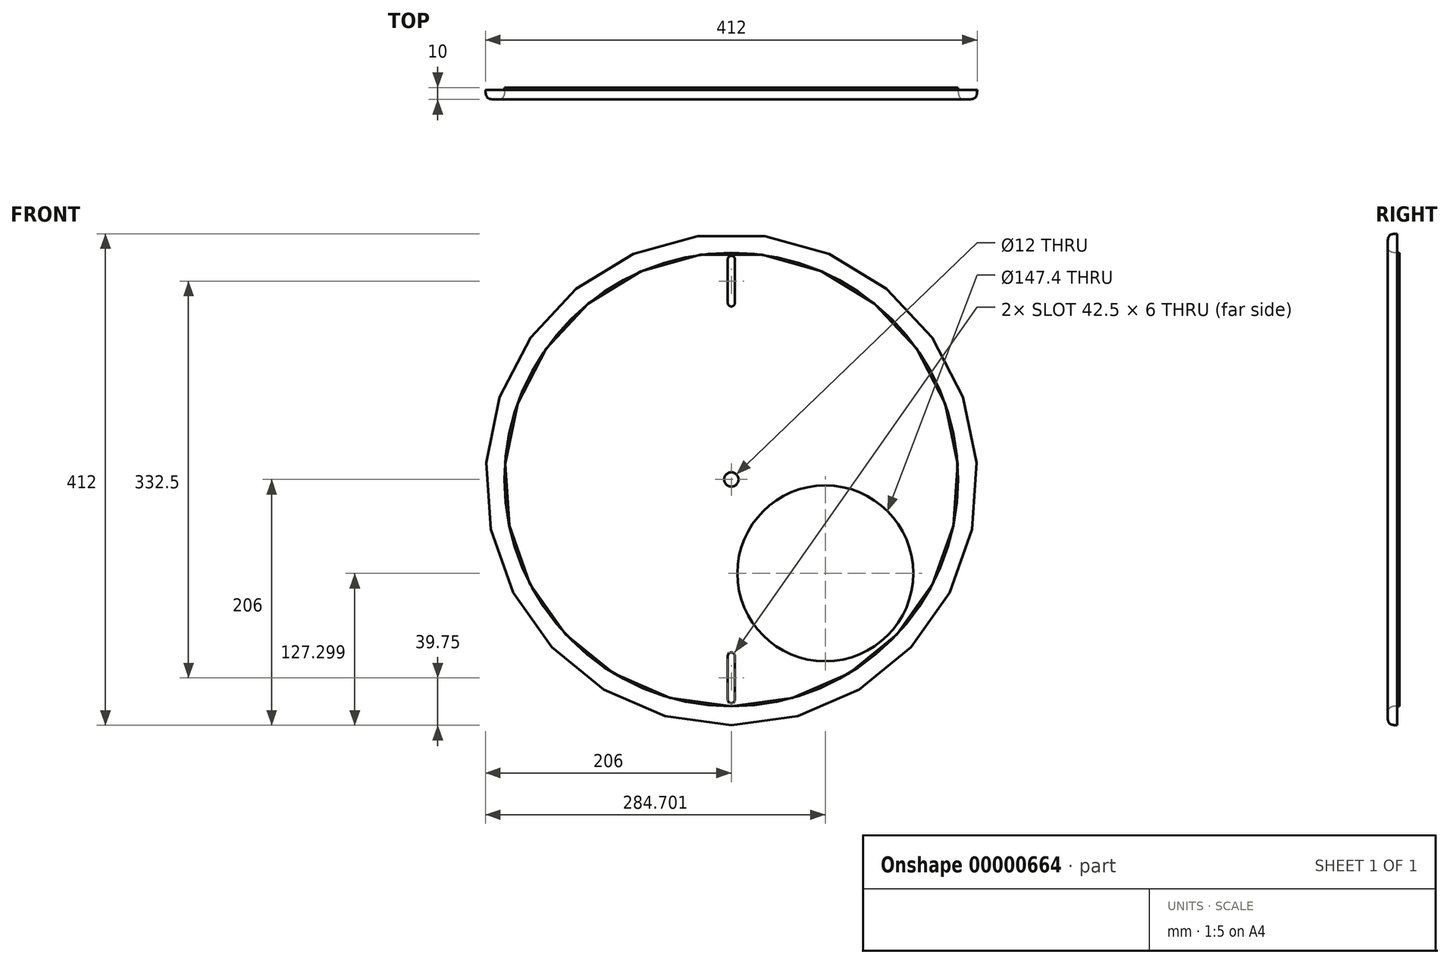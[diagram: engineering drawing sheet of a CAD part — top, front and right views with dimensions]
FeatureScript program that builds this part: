
annotation { "Feature Type Name" : "Feature", "Feature Type Description" : "" }
export const myFeature = defineFeature(function(context is Context, id is Id, definition is map)
    precondition{}
    {
        {
            var Q0;
            Q0=qCreatedBy(makeId("Front.planeOp"),FACE);
            var sketch = newSketch(context, id + "F0", { "sketchPlane" : qUnion([Q0])});
            skCircle(sketch, "E0", {"center": v(0, 0) * mm, "radius": 190 * mm});
            skCircle(sketch, "E1", {"center": v(0, 0) * mm, "radius": 6 * mm});
            skLineSegment(sketch, "E2", {"start": v(0, 190) * mm, "end": v(0, -190) * mm, "construction": true});
            skLineSegment(sketch, "E3", {"start": v(-190, 0) * mm, "end": v(190, 0) * mm, "construction": true});
            skCircle(sketch, "E4", {"center": v(78.7, -78.7) * mm, "radius": 78.7 * mm, "construction": true});
            skCircle(sketch, "E5", {"center": v(0, 0) * mm, "radius": 142.5 * mm, "construction": true});
            skCircle(sketch, "E6", {"center": v(0, 0) * mm, "radius": 145 * mm, "construction": true});
            skCircle(sketch, "E7", {"center": v(0, 0) * mm, "radius": 187.5 * mm, "construction": true});
            skLineSegment(sketch, "E8", {"start": v(0, 187.5) * mm, "end": v(0, 145) * mm, "construction": true});
            skLineSegment(sketch, "E9.rect.left", {"start": v(3, 184.5) * mm, "end": v(3, 148) * mm});
            skLineSegment(sketch, "E9.rect.right", {"start": v(-3, 184.5) * mm, "end": v(-3, 148) * mm});
            skPoint(sketch, "E9.rect.middle", {"position": v(0, 166.25) * mm});
            skArc(sketch, "E10", {"start": v(-3, 148) * mm, "mid": v(0, 145) * mm, "end": v(3, 148) * mm});
            skArc(sketch, "E11", {"start": v(3, 184.5) * mm, "mid": v(0, 187.5) * mm, "end": v(-3, 184.5) * mm});
            skPoint(sketch, "E12.orphan", {"position": v(3, 145.02) * mm});
            skPoint(sketch, "E13.orphan", {"position": v(-3, 145.02) * mm});
            skPoint(sketch, "E14.orphan", {"position": v(-3, 187.48) * mm});
            skPoint(sketch, "E15.orphan", {"position": v(3, 187.48) * mm});
            skArc(sketch, "E16.0.MirrorCS", {"start": v(-3, -148) * mm, "mid": v(0, -145) * mm, "end": v(3, -148) * mm});
            skArc(sketch, "E16.1.MirrorCS", {"start": v(3, -184.5) * mm, "mid": v(0, -187.5) * mm, "end": v(-3, -184.5) * mm});
            skLineSegment(sketch, "E16.2.MirrorCS", {"start": v(-3, -184.5) * mm, "end": v(-3, -148) * mm});
            skLineSegment(sketch, "E16.3.MirrorCS", {"start": v(3, -184.5) * mm, "end": v(3, -148) * mm});
            skCircle(sketch, "E17.0", {"center": v(78.7, -78.7) * mm, "radius": 73.7 * mm});
            skSolve(sketch);
        }
        {
            var Q0;
            Q0=makeQuery(id+"F0.imprint","IMPRINT",FACE,{"disambiguationData":[TD([[makeQuery(id+"F0.imprint","IMPRINT",EDGE,{"derivedFrom":sQuery(id+"F0.wireOp",EDGE,"E0")}),1.0]])]});
            extrude(context, id + "F1", {"entities" : qUnion([Q0]), "depth" : 2 * mm});
        }
        {
            var Q0;
            Q0=makeQuery(id+"F1.opExtrude","CAP_FACE",FACE,{"disambiguationData":[OSD([sQuery(id+"F0.wireOp",EDGE,"E0"),sQuery(id+"F0.wireOp",EDGE,"E1"),sQuery(id+"F0.wireOp",EDGE,"E9.rect.left"),sQuery(id+"F0.wireOp",EDGE,"E9.rect.right"),sQuery(id+"F0.wireOp",EDGE,"E10"),sQuery(id+"F0.wireOp",EDGE,"E11"),sQuery(id+"F0.wireOp",EDGE,"E16.3.MirrorCS"),sQuery(id+"F0.wireOp",EDGE,"E16.1.MirrorCS"),sQuery(id+"F0.wireOp",EDGE,"E16.2.MirrorCS"),sQuery(id+"F0.wireOp",EDGE,"E16.0.MirrorCS"),sQuery(id+"F0.wireOp",EDGE,"E17.0")])],"isStart":false});
            var sketch = newSketch(context, id + "F2", { "sketchPlane" : qUnion([Q0])});
            skCircle(sketch, "E18", {"center": v(0, 0) * mm, "radius": 190 * mm});
            skPoint(sketch, "E18.first.point", {"position": v(-140.07, 128.38) * mm});
            skPoint(sketch, "E18.second.point", {"position": v(165, 94.22) * mm});
            skPoint(sketch, "E18.third.point", {"position": v(77.15, -173.63) * mm});
            skCircle(sketch, "E19.0", {"center": v(0, 0) * mm, "radius": 206 * mm});
            skSolve(sketch);
        }
        {
            var Q0;
            Q0=makeQuery(id+"F2.imprint","IMPRINT",FACE,{"disambiguationData":[TD([[makeQuery(id+"F2.imprint","IMPRINT",EDGE,{"derivedFrom":sQuery(id+"F2.wireOp",EDGE,"E18")}),-1.0]])]});
            extrude(context, id + "F3", {"entities" : qUnion([Q0]), "depth" : 8 * mm});
        }
        {
            var Q0;
            Q0=makeQuery(id+"F3.opExtrude","CAP_EDGE",EDGE,{"disambiguationData":[OSD([sQuery(id+"F2.wireOp",EDGE,"E18")])],"isStart":false});
            var Q1;
            Q1=makeQuery(id+"F3.opExtrude","CAP_EDGE",EDGE,{"disambiguationData":[OSD([sQuery(id+"F2.wireOp",EDGE,"E19.0")])],"isStart":false});
            fillet(context, id + "F4", {"entities" : qUnion([Q0, Q1]), "radius" : 8 * mm, "tangentPropagation" : true, "rho" : 0.6, "crossSection" : FilletCrossSection.CONIC, "allowEdgeOverflow" : false});
        }
    });
